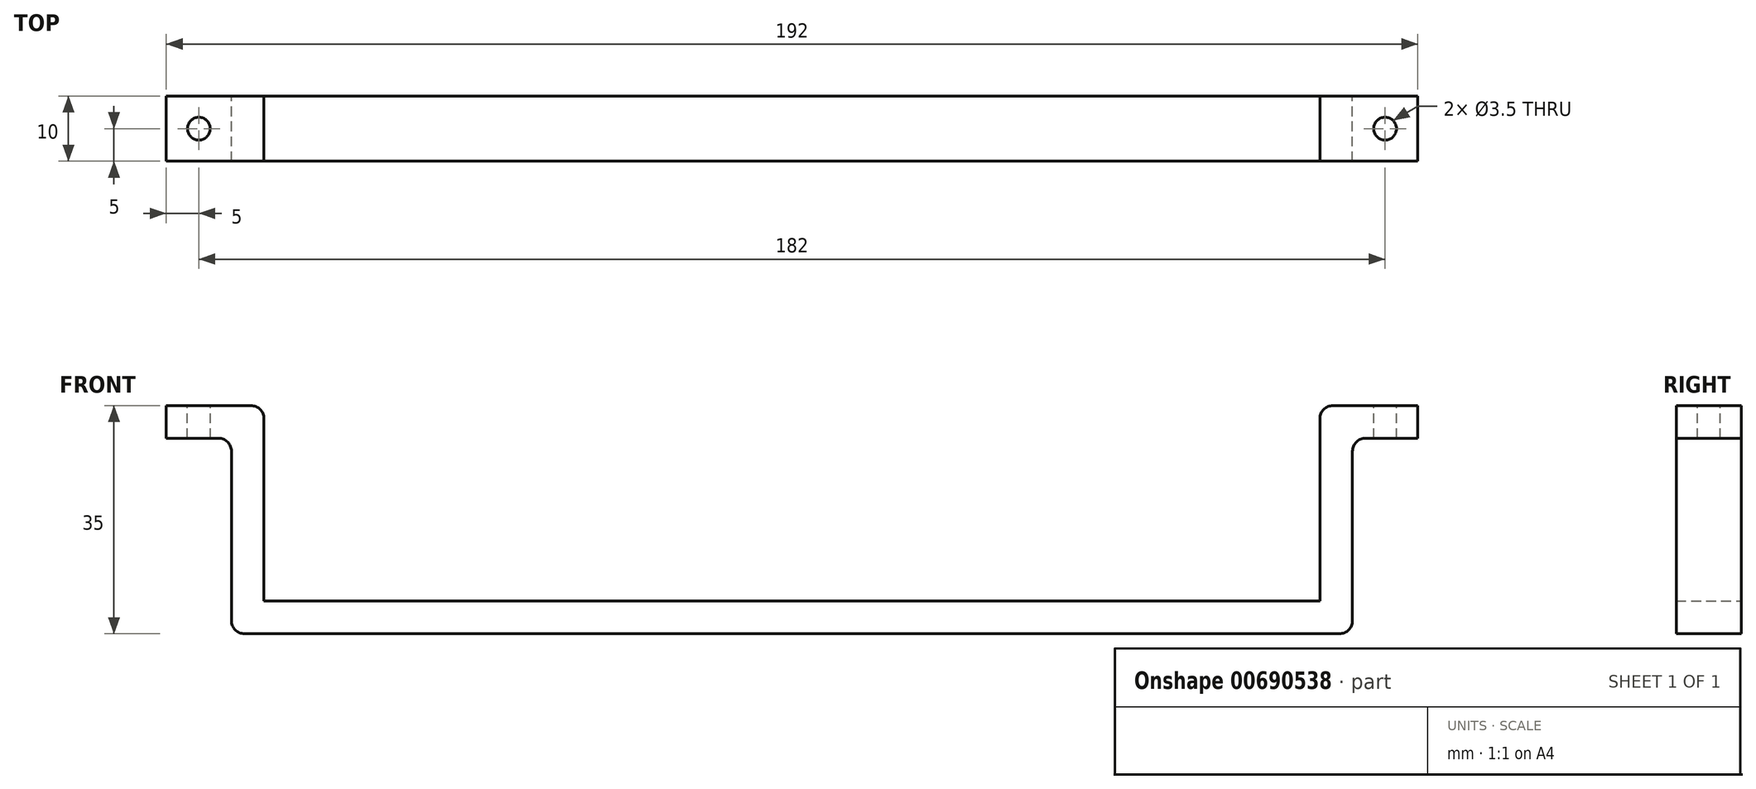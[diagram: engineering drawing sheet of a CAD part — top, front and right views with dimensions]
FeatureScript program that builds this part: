
annotation { "Feature Type Name" : "Feature", "Feature Type Description" : "" }
export const myFeature = defineFeature(function(context is Context, id is Id, definition is map)
    precondition{}
    {
        {
            var Q0;
            Q0=qCreatedBy(makeId("Front.planeOp"),FACE);
            var sketch = newSketch(context, id + "F0", { "sketchPlane" : qUnion([Q0])});
            skLineSegment(sketch, "E0.bottom", {"start": v(0, 0) * mm, "end": v(-81, 0) * mm});
            skLineSegment(sketch, "E0.top", {"start": v(0, 5) * mm, "end": v(-81, 5) * mm});
            skLineSegment(sketch, "E0.left", {"start": v(0, 0) * mm, "end": v(0, 5) * mm});
            skLineSegment(sketch, "E0.right", {"start": v(-81, 0) * mm, "end": v(-81, 5) * mm});
            skLineSegment(sketch, "E1.bottom", {"start": v(-81, 0) * mm, "end": v(-86, 0) * mm});
            skLineSegment(sketch, "E1.top", {"start": v(-81, 35) * mm, "end": v(-86, 35) * mm});
            skLineSegment(sketch, "E1.left", {"start": v(-81, 0) * mm, "end": v(-81, 35) * mm});
            skLineSegment(sketch, "E1.right", {"start": v(-86, 0) * mm, "end": v(-86, 35) * mm});
            skLineSegment(sketch, "E2.bottom", {"start": v(-86, 35) * mm, "end": v(-96, 35) * mm});
            skLineSegment(sketch, "E2.top", {"start": v(-86, 30) * mm, "end": v(-96, 30) * mm});
            skLineSegment(sketch, "E2.left", {"start": v(-86, 35) * mm, "end": v(-86, 30) * mm});
            skLineSegment(sketch, "E2.right", {"start": v(-96, 35) * mm, "end": v(-96, 30) * mm});
            skSolve(sketch);
        }
        {
            var Q0;
            Q0=makeQuery(id+"F0.imprint","IMPRINT",FACE,{"disambiguationData":[TD([[makeQuery(id+"F0.imprint","IMPRINT",EDGE,{"derivedFrom":sQuery(id+"F0.wireOp",EDGE,"E2.bottom")}),1.0]])]});
            var Q1;
            {var subQ3=sQuery(id+"F0.wireOp",EDGE,"E1.bottom");Q1=makeQuery(id+"F0.imprint","IMPRINT",FACE,{"disambiguationData":[TD([[makeQuery(id+"F0.imprint","IMPRINT",EDGE,{"derivedFrom":subQ3}),-1.0]])]});}
            var Q2;
            {var subQ0=sQuery(id+"F0.wireOp",EDGE,"E0.bottom");Q2=makeQuery(id+"F0.imprint","IMPRINT",FACE,{"disambiguationData":[TD([[makeQuery(id+"F0.imprint","IMPRINT",EDGE,{"derivedFrom":subQ0}),-1.0]])]});}
            extrude(context, id + "F1", {"entities" : qUnion([Q0, Q1, Q2]), "depth" : 10 * mm, "offsetDistance" : 25 * mm});
        }
        {
            var Q0;
            Q0=makeQuery(id+"F1.opExtrude","SWEPT_FACE",FACE,{"disambiguationData":[OSD([sQuery(id+"F0.wireOp",EDGE,"E1.top"),sQuery(id+"F0.wireOp",EDGE,"E2.bottom")])]});
            var sketch = newSketch(context, id + "F2", { "sketchPlane" : qUnion([Q0])});
            skLineSegment(sketch, "E3.0", {"start": v(-81, -10) * mm, "end": v(-81, 0) * mm});
            skLineSegment(sketch, "E3.1", {"start": v(-86, 0) * mm, "end": v(-96, 0) * mm});
            skLineSegment(sketch, "E3.2", {"start": v(-81, 0) * mm, "end": v(-86, 0) * mm});
            skLineSegment(sketch, "E3.3", {"start": v(-81, -10) * mm, "end": v(-96, -10) * mm});
            skLineSegment(sketch, "E3.4", {"start": v(-96, -10) * mm, "end": v(-96, 0) * mm});
            skCircle(sketch, "E4", {"center": v(-91, -5) * mm, "radius": 1.75 * mm});
            skLineSegment(sketch, "E5", {"start": v(-91, 0) * mm, "end": v(-91, -10) * mm, "construction": true});
            skSolve(sketch);
        }
        {
            var Q0;
            Q0=makeQuery(id+"F2.imprint","IMPRINT",FACE,{"disambiguationData":[TD([[makeQuery(id+"F2.imprint","IMPRINT",EDGE,{"derivedFrom":sQuery(id+"F2.wireOp",EDGE,"E4")}),1.0]])]});
            extrude(context, id + "F3", {"entities" : qUnion([Q0]), "operationType" : NewBodyOperationType.REMOVE, "endBound" : BoundingType.THROUGH_ALL, "oppositeDirection" : true, "depth" : 25 * mm, "offsetDistance" : 25 * mm});
        }
        {
            var Q0;
            Q0=makeQuery(id+"F1.opExtrude","SWEPT_EDGE",EDGE,{"disambiguationData":[OSD([sQuery(id+"F0.wireOp",EDGE,"E1.top"),sQuery(id+"F0.wireOp",EDGE,"E1.left")])]});
            var Q1;
            Q1=makeQuery(id+"F1.opExtrude","SWEPT_EDGE",EDGE,{"disambiguationData":[OSD([sQuery(id+"F0.wireOp",EDGE,"E1.right"),sQuery(id+"F0.wireOp",EDGE,"E2.top"),sQuery(id+"F0.wireOp",EDGE,"E2.left")])]});
            var Q2;
            Q2=makeQuery(id+"F1.opExtrude","SWEPT_EDGE",EDGE,{"disambiguationData":[OSD([sQuery(id+"F0.wireOp",EDGE,"E1.bottom"),sQuery(id+"F0.wireOp",EDGE,"E1.right")])]});
            fillet(context, id + "F4", {"entities" : qUnion([Q0, Q1, Q2]), "radius" : 2 * mm, "tangentPropagation" : true, "allowEdgeOverflow" : false});
        }
        {
            var Q0;
            Q0=makeQuery(id+"F1.opExtrude","SWEPT_BODY",BODY,{"disambiguationData":[OSD([sQuery(id+"F0.wireOp",EDGE,"E0.bottom"),sQuery(id+"F0.wireOp",EDGE,"E0.top"),sQuery(id+"F0.wireOp",EDGE,"E0.left"),sQuery(id+"F0.wireOp",EDGE,"E1.bottom"),sQuery(id+"F0.wireOp",EDGE,"E1.top"),sQuery(id+"F0.wireOp",EDGE,"E1.left"),sQuery(id+"F0.wireOp",EDGE,"E1.right"),sQuery(id+"F0.wireOp",EDGE,"E2.bottom"),sQuery(id+"F0.wireOp",EDGE,"E2.top"),sQuery(id+"F0.wireOp",EDGE,"E2.right")])]});
            var Q1;
            Q1=qCreatedBy(makeId("Right.planeOp"),FACE);
            mirror(context, id + "F5", {"operationType" : NewBodyOperationType.ADD, "entities" : qUnion([Q0]), "mirrorPlane" : qUnion([Q1])});
        }
    });
